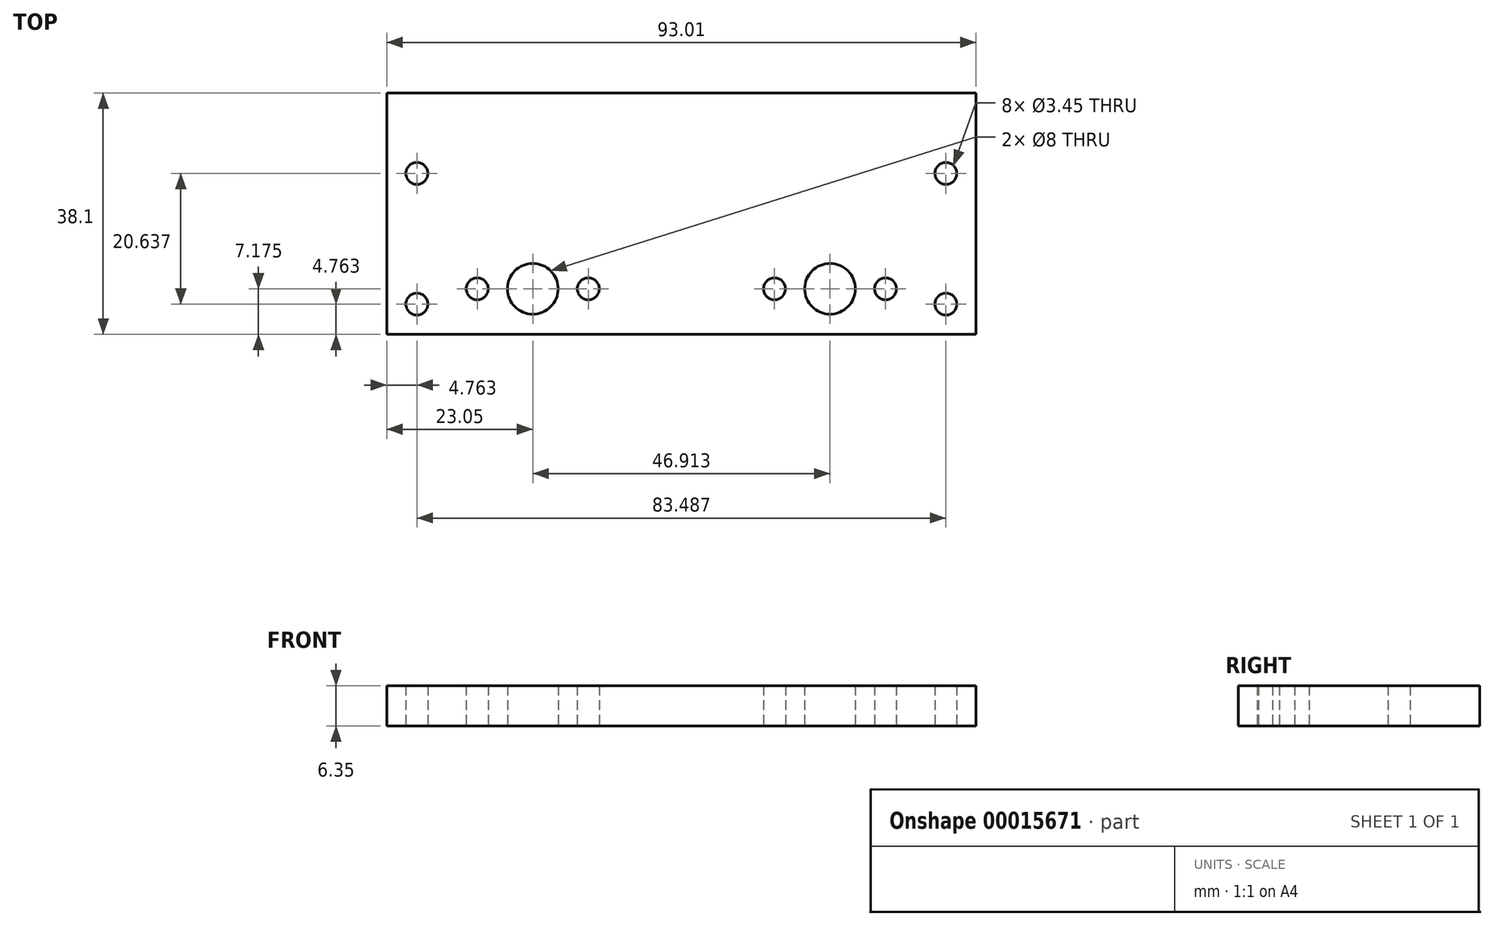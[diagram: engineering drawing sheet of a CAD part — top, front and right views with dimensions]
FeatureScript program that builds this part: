
annotation { "Feature Type Name" : "Feature", "Feature Type Description" : "" }
export const myFeature = defineFeature(function(context is Context, id is Id, definition is map)
    precondition{}
    {
        {
            var Q0;
            Q0=qCreatedBy(makeId("Top.planeOp"),FACE);
            var sketch = newSketch(context, id + "F0", { "sketchPlane" : qUnion([Q0])});
            skLineSegment(sketch, "E0.bottom", {"start": v(0, 0) * mm, "end": v(93.01, 0) * mm});
            skLineSegment(sketch, "E0.top", {"start": v(0, -38.1) * mm, "end": v(93.01, -38.1) * mm});
            skLineSegment(sketch, "E0.left", {"start": v(0, 0) * mm, "end": v(0, -38.1) * mm});
            skLineSegment(sketch, "E0.right", {"start": v(93.01, 0) * mm, "end": v(93.01, -38.1) * mm});
            skLineSegment(sketch, "E1", {"start": v(23.05, 0) * mm, "end": v(23.05, -30.92) * mm});
            skLineSegment(sketch, "E2", {"start": v(69.96, 0) * mm, "end": v(69.96, -30.92) * mm});
            skLineSegment(sketch, "E3", {"start": v(61.2, -30.92) * mm, "end": v(78.73, -30.92) * mm});
            skLineSegment(sketch, "E4", {"start": v(14.29, -30.92) * mm, "end": v(31.81, -30.92) * mm});
            skCircle(sketch, "E5", {"center": v(14.29, -30.92) * mm, "radius": 1.73 * mm});
            skCircle(sketch, "E6", {"center": v(23.05, -30.92) * mm, "radius": 4 * mm});
            skCircle(sketch, "E7", {"center": v(31.81, -30.92) * mm, "radius": 1.73 * mm});
            skCircle(sketch, "E8", {"center": v(61.2, -30.92) * mm, "radius": 1.73 * mm});
            skCircle(sketch, "E9", {"center": v(78.73, -30.92) * mm, "radius": 1.73 * mm});
            skCircle(sketch, "E10", {"center": v(69.96, -30.92) * mm, "radius": 4 * mm});
            skLineSegment(sketch, "E11", {"start": v(23.05, -30.92) * mm, "end": v(23.05, -38.1) * mm});
            skLineSegment(sketch, "E12", {"start": v(88.25, 0) * mm, "end": v(88.25, -12.7) * mm});
            skLineSegment(sketch, "E13", {"start": v(88.25, -12.7) * mm, "end": v(88.25, -33.34) * mm});
            skLineSegment(sketch, "E14", {"start": v(4.76, -33.34) * mm, "end": v(4.76, -12.7) * mm});
            skLineSegment(sketch, "E15", {"start": v(4.76, -12.7) * mm, "end": v(4.76, 0) * mm});
            skCircle(sketch, "E16", {"center": v(88.25, -33.34) * mm, "radius": 1.73 * mm});
            skCircle(sketch, "E17", {"center": v(88.25, -12.7) * mm, "radius": 1.73 * mm});
            skCircle(sketch, "E18", {"center": v(4.76, -12.7) * mm, "radius": 1.73 * mm});
            skCircle(sketch, "E19", {"center": v(4.76, -33.34) * mm, "radius": 1.73 * mm});
            skLineSegment(sketch, "E20", {"start": v(78.73, -30.92) * mm, "end": v(88.25, -30.92) * mm});
            skLineSegment(sketch, "E21", {"start": v(88.25, -30.92) * mm, "end": v(93.01, -30.92) * mm});
            skLineSegment(sketch, "E22", {"start": v(14.29, -30.92) * mm, "end": v(4.76, -30.92) * mm});
            skLineSegment(sketch, "E23", {"start": v(4.76, -30.92) * mm, "end": v(0, -30.92) * mm});
            skSolve(sketch);
        }
        {
            var Q0;
            Q0 = qSketchRegion(id + "F0", true);
            extrude(context, id + "F1", {"entities" : qUnion([Q0]), "depth" : 6.35 * mm});
        }
    });
